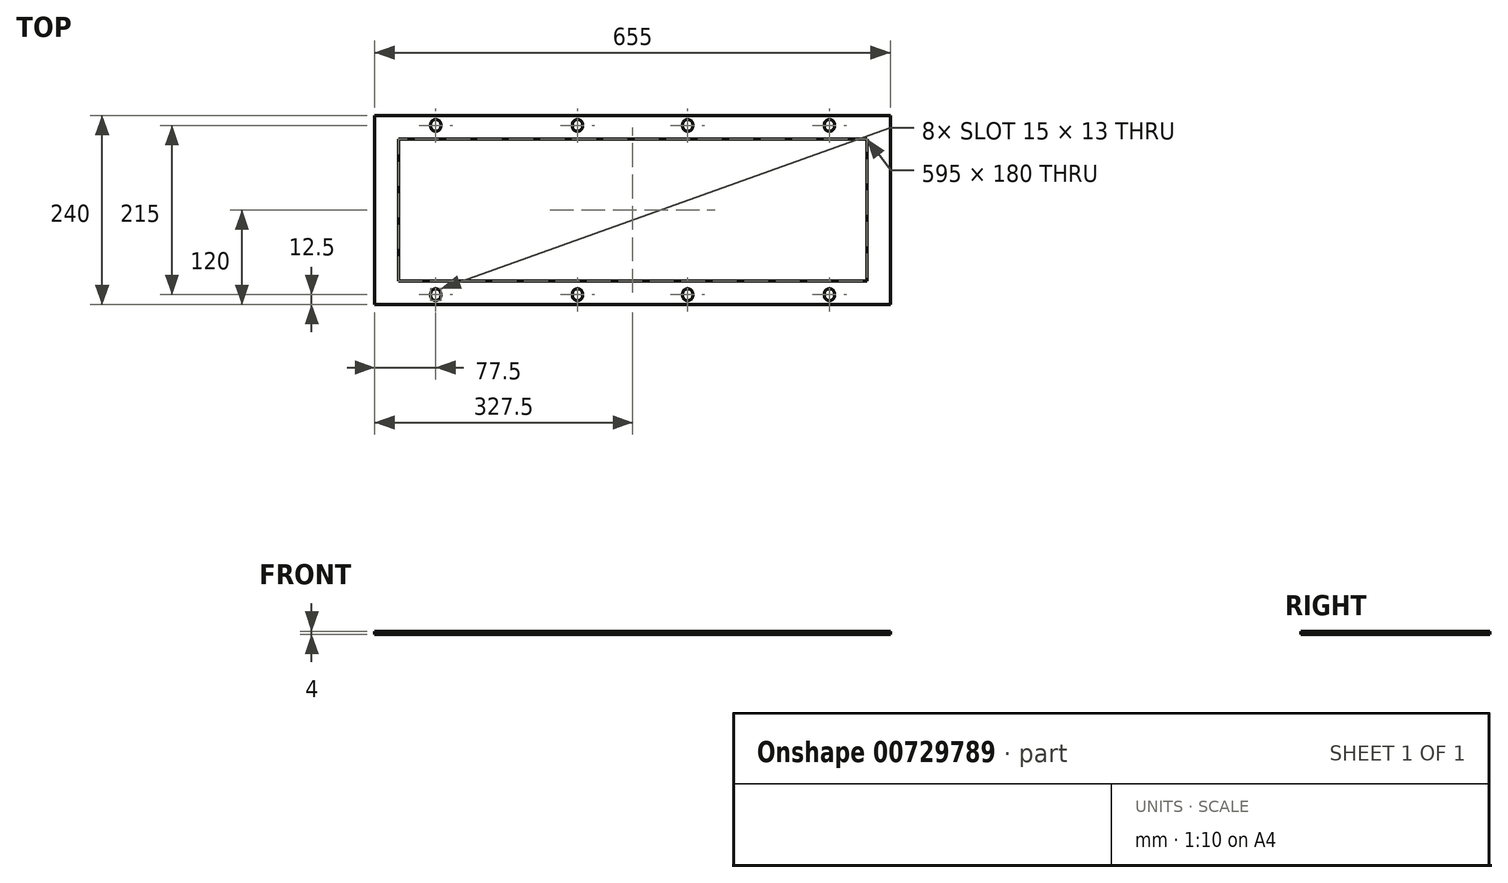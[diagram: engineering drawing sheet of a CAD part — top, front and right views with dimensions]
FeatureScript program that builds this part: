
annotation { "Feature Type Name" : "Feature", "Feature Type Description" : "" }
export const myFeature = defineFeature(function(context is Context, id is Id, definition is map)
    precondition{}
    {
        {
            var Q0;
            Q0=qCreatedBy(makeId("Top.planeOp"),FACE);
            var sketch = newSketch(context, id + "F0", { "sketchPlane" : qUnion([Q0])});
            skLineSegment(sketch, "E0", {"start": v(0, 0) * mm, "end": v(655, 0) * mm});
            skLineSegment(sketch, "E1", {"start": v(655, 0) * mm, "end": v(655, 240) * mm});
            skLineSegment(sketch, "E2", {"start": v(655, 240) * mm, "end": v(0, 240) * mm});
            skLineSegment(sketch, "E3", {"start": v(0, 240) * mm, "end": v(0, 0) * mm});
            skLineSegment(sketch, "E4", {"start": v(30, 30) * mm, "end": v(30, 210) * mm});
            skLineSegment(sketch, "E5", {"start": v(30, 210) * mm, "end": v(625, 210) * mm});
            skLineSegment(sketch, "E6", {"start": v(625, 210) * mm, "end": v(625, 30) * mm});
            skLineSegment(sketch, "E7", {"start": v(625, 30) * mm, "end": v(30, 30) * mm});
            skLineSegment(sketch, "E8", {"start": v(77.5, 228.5) * mm, "end": v(77.5, 226.5) * mm, "construction": true});
            skLineSegment(sketch, "E9", {"start": v(77.5, 226.5) * mm, "end": v(77.5, 227.5) * mm, "construction": true});
            skCircle(sketch, "E10", {"center": v(77.5, 228.5) * mm, "radius": 6.5 * mm});
            skCircle(sketch, "E11", {"center": v(77.5, 226.5) * mm, "radius": 6.5 * mm});
            skLineSegment(sketch, "E12", {"start": v(71, 228.5) * mm, "end": v(71, 226.5) * mm});
            skLineSegment(sketch, "E13", {"start": v(84, 228.5) * mm, "end": v(84, 226.5) * mm});
            skLineSegment(sketch, "E14", {"start": v(257.5, 228.5) * mm, "end": v(257.5, 226.5) * mm, "construction": true});
            skLineSegment(sketch, "E15", {"start": v(257.5, 226.5) * mm, "end": v(257.5, 227.5) * mm, "construction": true});
            skCircle(sketch, "E16", {"center": v(257.5, 228.5) * mm, "radius": 6.5 * mm});
            skCircle(sketch, "E17", {"center": v(257.5, 226.5) * mm, "radius": 6.5 * mm});
            skLineSegment(sketch, "E18", {"start": v(251, 228.5) * mm, "end": v(251, 226.5) * mm});
            skLineSegment(sketch, "E19", {"start": v(264, 228.5) * mm, "end": v(264, 226.5) * mm});
            skLineSegment(sketch, "E20", {"start": v(327.5, 240) * mm, "end": v(327.5, 0) * mm, "construction": true});
            skLineSegment(sketch, "E21", {"start": v(655, 120) * mm, "end": v(0, 120) * mm, "construction": true});
            skLineSegment(sketch, "E22.MirrorCS", {"start": v(577.5, 226.5) * mm, "end": v(577.5, 227.5) * mm, "construction": true});
            skLineSegment(sketch, "E23.MirrorCS", {"start": v(577.5, 228.5) * mm, "end": v(577.5, 226.5) * mm, "construction": true});
            skLineSegment(sketch, "E24.MirrorCS", {"start": v(397.5, 228.5) * mm, "end": v(397.5, 226.5) * mm, "construction": true});
            skLineSegment(sketch, "E25.MirrorCS", {"start": v(397.5, 226.5) * mm, "end": v(397.5, 227.5) * mm, "construction": true});
            skLineSegment(sketch, "E26.MirrorCS", {"start": v(584, 228.5) * mm, "end": v(584, 226.5) * mm});
            skLineSegment(sketch, "E27.MirrorCS", {"start": v(571, 228.5) * mm, "end": v(571, 226.5) * mm});
            skLineSegment(sketch, "E28.MirrorCS", {"start": v(391, 228.5) * mm, "end": v(391, 226.5) * mm});
            skLineSegment(sketch, "E29.MirrorCS", {"start": v(404, 228.5) * mm, "end": v(404, 226.5) * mm});
            skCircle(sketch, "E30.MirrorC", {"center": v(577.5, 226.5) * mm, "radius": 6.5 * mm});
            skCircle(sketch, "E31.MirrorC", {"center": v(397.5, 226.5) * mm, "radius": 6.5 * mm});
            skCircle(sketch, "E32.MirrorC", {"center": v(577.5, 228.5) * mm, "radius": 6.5 * mm});
            skCircle(sketch, "E33.MirrorC", {"center": v(397.5, 228.5) * mm, "radius": 6.5 * mm});
            skLineSegment(sketch, "E34.MirrorCS", {"start": v(264, 11.5) * mm, "end": v(264, 13.5) * mm});
            skLineSegment(sketch, "E35.MirrorCS", {"start": v(77.5, 11.5) * mm, "end": v(77.5, 13.5) * mm, "construction": true});
            skLineSegment(sketch, "E36.MirrorCS", {"start": v(257.5, 11.5) * mm, "end": v(257.5, 13.5) * mm, "construction": true});
            skLineSegment(sketch, "E37.MirrorCS", {"start": v(84, 11.5) * mm, "end": v(84, 13.5) * mm});
            skLineSegment(sketch, "E38.MirrorCS", {"start": v(251, 11.5) * mm, "end": v(251, 13.5) * mm});
            skLineSegment(sketch, "E39.MirrorCS", {"start": v(77.5, 13.5) * mm, "end": v(77.5, 12.5) * mm, "construction": true});
            skCircle(sketch, "E40.MirrorC", {"center": v(77.5, 11.5) * mm, "radius": 6.5 * mm});
            skCircle(sketch, "E41.MirrorC", {"center": v(257.5, 11.5) * mm, "radius": 6.5 * mm});
            skCircle(sketch, "E42.MirrorC", {"center": v(77.5, 13.5) * mm, "radius": 6.5 * mm});
            skLineSegment(sketch, "E43.MirrorCS", {"start": v(71, 11.5) * mm, "end": v(71, 13.5) * mm});
            skLineSegment(sketch, "E44.MirrorCS", {"start": v(584, 11.5) * mm, "end": v(584, 13.5) * mm});
            skLineSegment(sketch, "E45.MirrorCS", {"start": v(571, 11.5) * mm, "end": v(571, 13.5) * mm});
            skCircle(sketch, "E46.MirrorC", {"center": v(257.5, 13.5) * mm, "radius": 6.5 * mm});
            skLineSegment(sketch, "E47.MirrorCS", {"start": v(577.5, 11.5) * mm, "end": v(577.5, 13.5) * mm, "construction": true});
            skLineSegment(sketch, "E48.MirrorCS", {"start": v(404, 11.5) * mm, "end": v(404, 13.5) * mm});
            skLineSegment(sketch, "E49.MirrorCS", {"start": v(257.5, 13.5) * mm, "end": v(257.5, 12.5) * mm, "construction": true});
            skLineSegment(sketch, "E50.MirrorCS", {"start": v(391, 11.5) * mm, "end": v(391, 13.5) * mm});
            skLineSegment(sketch, "E51.MirrorCS", {"start": v(397.5, 11.5) * mm, "end": v(397.5, 13.5) * mm, "construction": true});
            skLineSegment(sketch, "E52.MirrorCS", {"start": v(577.5, 13.5) * mm, "end": v(577.5, 12.5) * mm, "construction": true});
            skLineSegment(sketch, "E53.MirrorCS", {"start": v(397.5, 13.5) * mm, "end": v(397.5, 12.5) * mm, "construction": true});
            skCircle(sketch, "E54.MirrorC", {"center": v(397.5, 11.5) * mm, "radius": 6.5 * mm});
            skCircle(sketch, "E55.MirrorC", {"center": v(577.5, 11.5) * mm, "radius": 6.5 * mm});
            skCircle(sketch, "E56.MirrorC", {"center": v(577.5, 13.5) * mm, "radius": 6.5 * mm});
            skCircle(sketch, "E57.MirrorC", {"center": v(397.5, 13.5) * mm, "radius": 6.5 * mm});
            skSolve(sketch);
        }
        {
            var Q0;
            Q0 = qSketchRegion(id + "F0", true);
            extrude(context, id + "F1", {"entities" : qUnion([Q0]), "depth" : 4 * mm, "offsetDistance" : 25 * mm});
        }
    });
